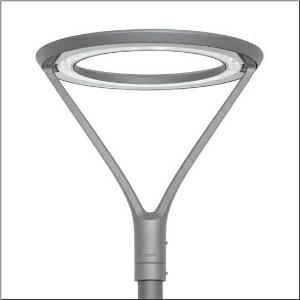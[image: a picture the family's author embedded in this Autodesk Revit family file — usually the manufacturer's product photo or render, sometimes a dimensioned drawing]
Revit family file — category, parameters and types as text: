
# Revit family: dl_r__20___pl1_2s_5xa512836s008p_4065
name_source: partatom
category: Lighting Fixtures
units: mm (PartAtom-declared; Revit-internal decimal feet)

## family parameters
Cut with Voids When Loaded = No
Host = Face
Light Source = No
Part Type = Normal
Room Calculation Point = No
Round Connector Dimension = Use Diameter
Shared = No

## types (1)
- --- (1 x LED, 4250 lm, 40.6 W, 2700K)
    Apparent Load = 41 VA
    CIE Flux Codes = 33 78 99 100 100
    Color Rendering = 70
    Color Temperature = 2700K
    Default Elevation = 1800 mm
    Description = DL® 20, mast luminaire, primary light control with reflector, highly specular, primary optical cover: cover, of toughened safety glass of clear glass with excellent transmission level, light distribution: PL1.2s, light emission: direct distribution, primary light characteristic: symmetric, installation type: post-top, LED, High Power LED, rated luminous flux: 4.250lm, luminous efficacy: 105lm/W, light colour: 727, colour temperature: 2700K, control gear: Plus, control: flexible luminous flux parameterisation, time-dependent luminous flux control, constant luminous flux control, digital communication interface, power reduction, overheat protection, electronic power reduction, mains connection: 220..240V, 50/60Hz, connection cable pre-assembled, cable length: 5m, start of lifetime: 41W, end of service life: 42W, reduction: 20W, luminaire housing, upper part, of cast aluminium, powder-coated, Siteco® metallic grey (DB 702S), diameter: 690mm, height: 690mm, spigot size: 76mm (post-top), mounting height: 4..6m, luminaire housing, of cast aluminium, powder-coated, Siteco® metallic grey (DB 702S), equipment: Power, protection rating (complete): IP66, insulation class (complete): insulation class II (safety insulation), certification: CE, ENEC, VDE, impact resistance: IK08, permissible operating ambient temperature: -25..+30°C, standard-compliant lighting for roads and squares, packaging unit: 1 piece

Light Distribution: PL1.2s
    Height = 690 mm
    Lamp = 1 x LED
    Lamp Light Flux = 4250 lm
    Lamp Power = 40.6 W
    Lamp count = 1
    Length = 690 mm
    Luminous efficacy = 105 lm/W
    Manufacturer = Siteco
    ModVariant = No
    Model = 5XA512836S008P
    Number of Poles = 1
    OnlyDefault = Yes
    Power Factor = 1
    Product Name = DL® 20 | PL1.2s
    Product group = mast luminaire | pylon top
    ProductGroupID = 6100
    Protection Class = Protection class II
    Protection Degree = IP 66
    RLX_Detail_Level = 1
    RLX_Emergency_Light_Flux = 0 lm
    RLX_Emergency_Type = 0
    RLX_Emergency_Type_DB = No
    RlxData = <blob elided: 204377 chars, md5=c1b8c603>
    Socket = socket
    Standby Power = 0 W
    System Light Flux = 4250 lm
    System Power = 41 W
    Type Comments = factory setting: luminous flux: 100 % | dim-lin: 254 | 549 mA
    Type Image = l_1006001.jpg
    URL = http://relux.com
    VarID = @adj_076790
    Voltage = 0 V
    Weight = 0.00 kg
    Width = 0 mm  [stored 0 ft]

note: [stored X ft] marks values corroborated as IEEE doubles in the binary element streams (Revit-internal decimal feet)

## geometry (parser evidence)
native form markers: Blend x4, Sweep x10
no freeform markers — native parametric forms only
